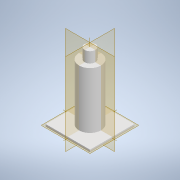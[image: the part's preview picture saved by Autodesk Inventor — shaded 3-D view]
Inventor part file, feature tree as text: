
AUTODESK INVENTOR PART (.ipt)
format: ipt  version: 2022.4 (Build 264492010, 492A)  size: 131,072 bytes
history: native  units: mm
features: extrude x4, sketch x4
ambient origin geometry x8: Origin, YZ Plane, XZ Plane, XY Plane, X Axis, Y Axis, Z Axis, Center Point
bodies: Solid1 (feature_tree)
feature tree (8):
  extrude  "Extrusion1"  Depth=20.0mm
  extrude  "Extrusion2"  Depth=5.0mm
  extrude  "Extrusion3"  Depth=5.0mm
  extrude  "Extrusion4"  Depth=2.5mm TaperAngle=0.0deg
  sketch  "Sketch1"  dims[d0=20.0mm d1=20.0mm]
  sketch  "Sketch2"  dims[d2=1.0mm d3=0.0mm d4=5.0mm]
  sketch  "Sketch3"  dims[d5=5.0mm d6=5.0mm]
  sketch  "Sketch7"  dims[d7=20.0mm d9=360.0deg d11=2.5mm d12=0.0mm d13=10.0mm d14=25.0mm d15=0.0mm d50=5.0mm d51=5.0mm d52=0.0mm]
